# Revit family: Pearl Single 5W
name_source: partatom
category: Lighting Fixtures
units: mm (PartAtom-declared; Revit-internal decimal feet)

## family parameters
Cut with Voids When Loaded = No
Host = Face
Light Source = No
OmniClass Number = 23.80.70.11.11
OmniClass Title = General Luminaries, Non Directional
Part Type = Normal
Room Calculation Point = No
Round Connector Dimension = Use Diameter
Shared = No

## types (2) — shared parameters
CRI = 82
Casing Color = White
Cutout = -
Default Elevation = 1219 mm
Depth = -
Description = Pendant Light
Dimensions = 86mm x 1600mm
Dimmable = Yes
Directivity = No
Driver = Integrated
Housing Material = Aluminium
IP Code = IP20
Lamp = LED
Last Updated = 8.3.2017
Lifetime L70 = 50000h
Manufacturer = Winled Oy Ltd
Operating Temperature Range = -20° to +50°
Type Image = Pearl Single .png
URL = www.winled.fi
Voltage = 230 V
Wattage Comments = 5W

## per-type parameters (varying)
| type | Beam Angle | Color Temperature | Light source | Lumens Output | Model | Product Number |
| Pearl Single 5W, Neutral White, 230V - 53SI995N005J | 160° | 4000K | Pearl light NV | 488lm | Pear Single 5W | 53SI995N005J |
| Pearl Single 5W, Warm White, 230V - 53SI995L005J | 90° | 3000K | Pearl light LV | 388lm | Pearl Single 5W | 53SI995L005J |

## geometry (parser evidence)
native form markers: Sweep x13
no freeform markers — native parametric forms only
